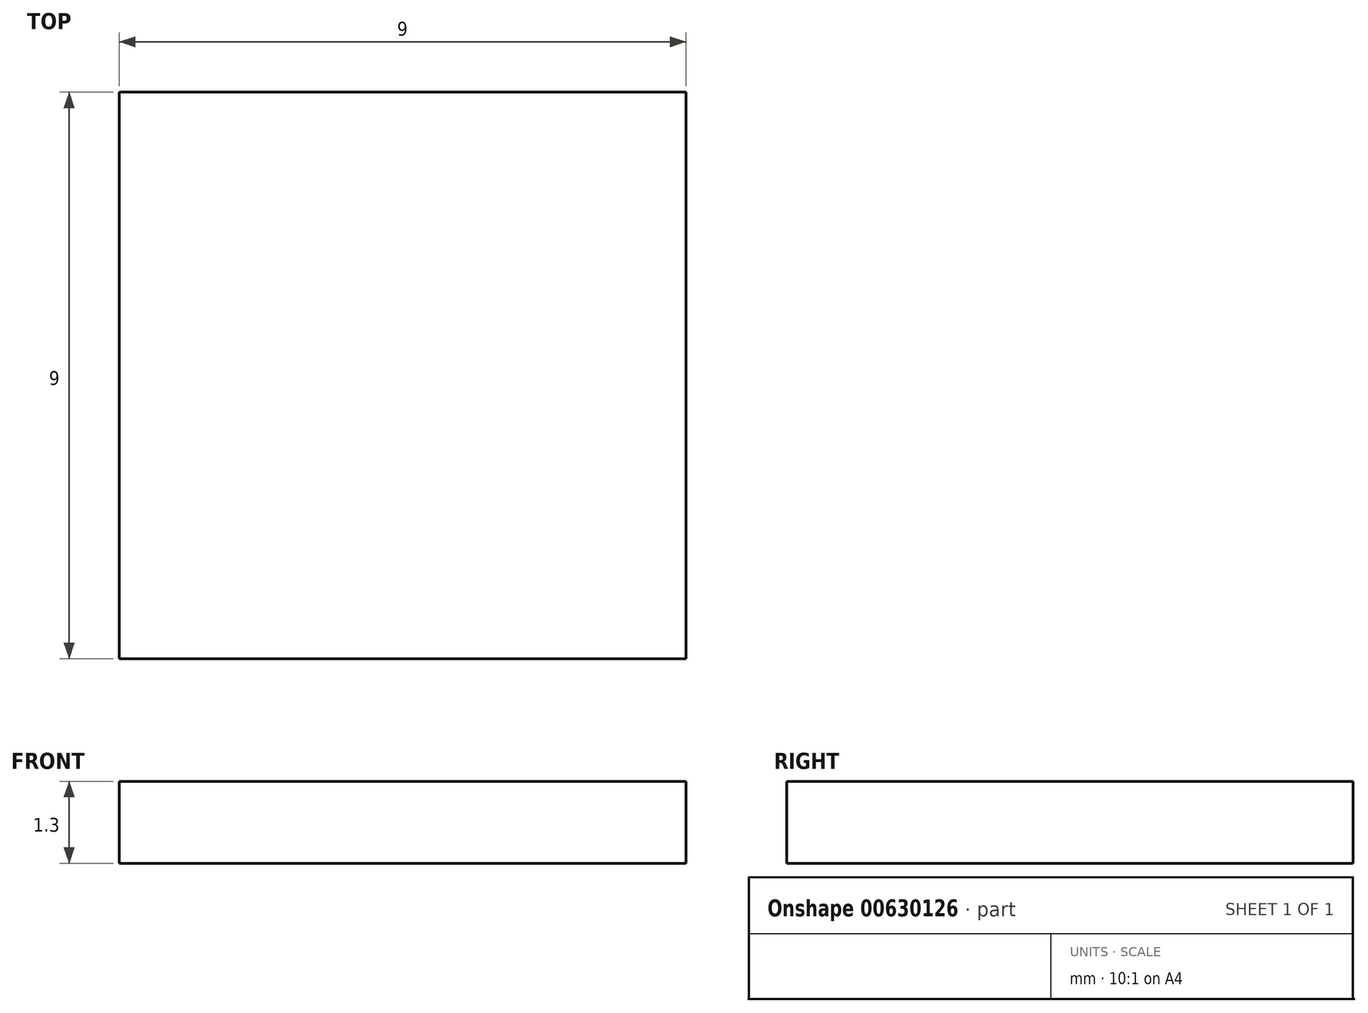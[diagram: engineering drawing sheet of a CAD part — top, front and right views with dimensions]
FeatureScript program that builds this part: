
annotation { "Feature Type Name" : "Feature", "Feature Type Description" : "" }
export const myFeature = defineFeature(function(context is Context, id is Id, definition is map)
    precondition{}
    {
        {
            var Q0;
            Q0=qCreatedBy(makeId("Top.planeOp"),FACE);
            var sketch = newSketch(context, id + "F0", { "sketchPlane" : qUnion([Q0])});
            skLineSegment(sketch, "E0.bottom", {"start": v(0, 0) * mm, "end": v(9, 0) * mm});
            skLineSegment(sketch, "E0.top", {"start": v(0, 9) * mm, "end": v(9, 9) * mm});
            skLineSegment(sketch, "E0.left", {"start": v(0, 0) * mm, "end": v(0, 9) * mm});
            skLineSegment(sketch, "E0.right", {"start": v(9, 0) * mm, "end": v(9, 9) * mm});
            skSolve(sketch);
        }
        {
            var Q0;
            Q0=qSketchRegion(id+"F0",true);
            extrude(context, id + "F1", {"entities" : qUnion([Q0]), "depth" : 1.3 * mm});
        }
    });
